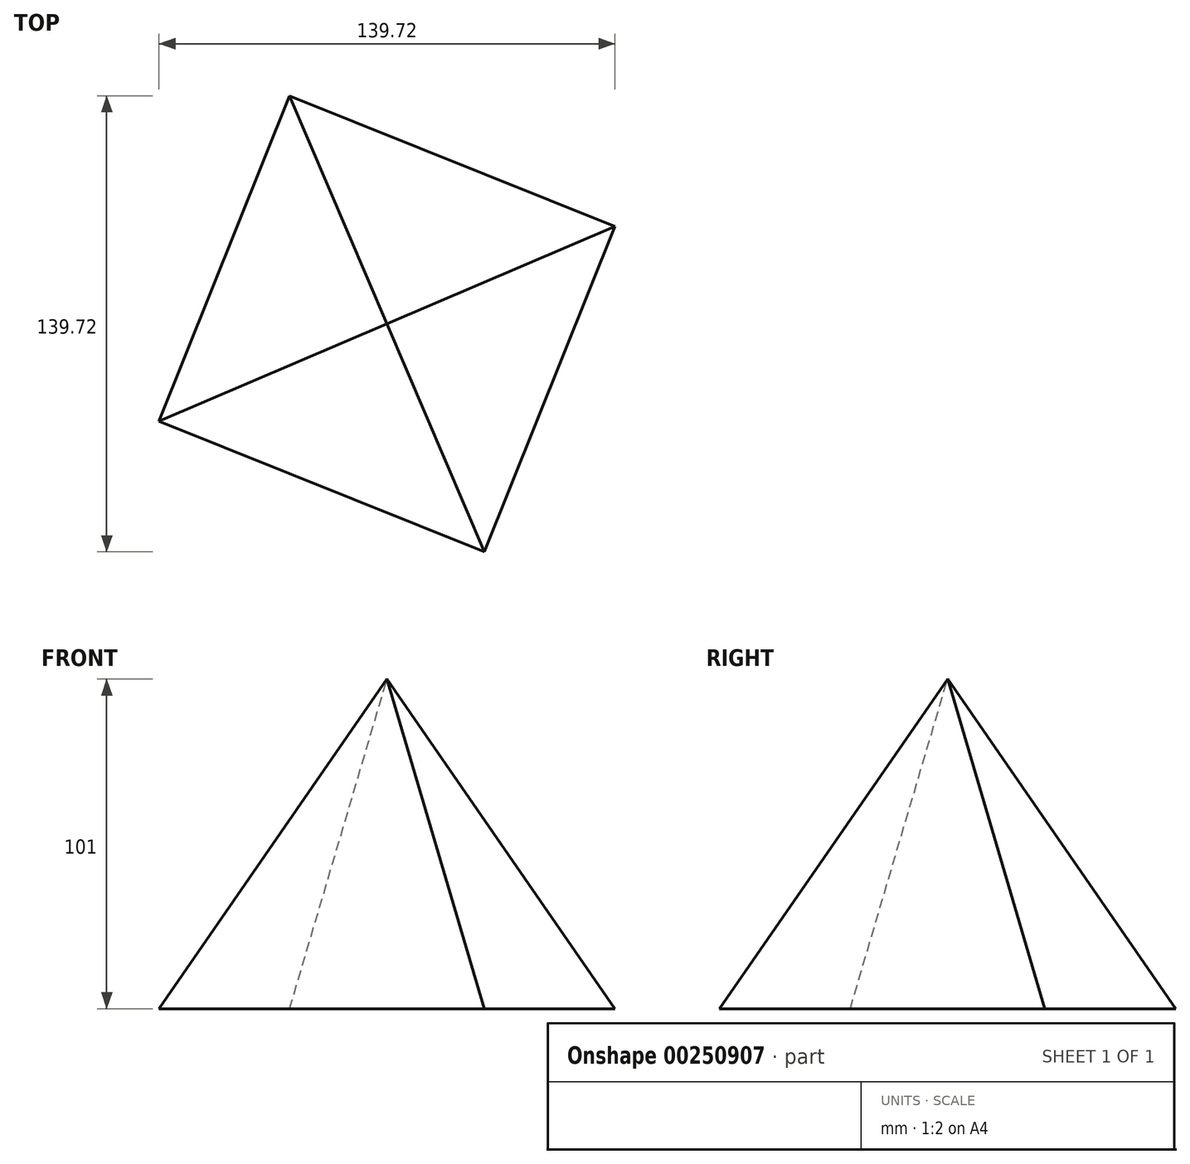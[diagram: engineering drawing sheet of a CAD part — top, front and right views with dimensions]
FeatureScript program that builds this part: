
annotation { "Feature Type Name" : "Feature", "Feature Type Description" : "" }
export const myFeature = defineFeature(function(context is Context, id is Id, definition is map)
    precondition{}
    {
        {
            var Q0;
            Q0=qCreatedBy(makeId("Top.planeOp"),FACE);
            var sketch = newSketch(context, id + "F0", { "sketchPlane" : qUnion([Q0])});
            skCircle(sketch, "E0.cCircle", {"center": v(0, 0) * mm, "radius": 75.96 * mm, "construction": true});
            skLineSegment(sketch, "E0.0", {"start": v(29.84, -69.86) * mm, "end": v(-69.86, -29.84) * mm});
            skLineSegment(sketch, "E0.1", {"start": v(-69.86, -29.84) * mm, "end": v(-29.84, 69.86) * mm});
            skLineSegment(sketch, "E0.2", {"start": v(-29.84, 69.86) * mm, "end": v(69.86, 29.84) * mm});
            skLineSegment(sketch, "E0.3", {"start": v(69.86, 29.84) * mm, "end": v(29.84, -69.86) * mm});
            skSolve(sketch);
        }
        {
            var Q0;
            Q0=qCreatedBy(makeId("Top.planeOp"),FACE);
            cPlane(context, id + "F1", {"entities" : qUnion([Q0]), "cplaneType" : CPlaneType.OFFSET, "offset" : 101 * mm, "width" : 150 * mm, "height" : 150 * mm});
        }
        {
            var Q0;
            Q0=qCreatedBy(id+"F1.planeOp",FACE);
            var sketch = newSketch(context, id + "F2", { "sketchPlane" : qUnion([Q0])});
            skPoint(sketch, "E1", {"position": v(0, 0) * mm});
            skSolve(sketch);
        }
        {
            var Q0;
            Q0 = qSketchRegion(id + "F0", true);
            var Q1;
            Q1=sQuery(id+"F2.wireOp",VERTEX,"E1");
            loft(context, id + "F3", {"sheetProfilesArray" : [{ "sheetProfileEntities" : qUnion([Q0]) }, { "sheetProfileEntities" : qUnion([Q1]) }]});
        }
    });
